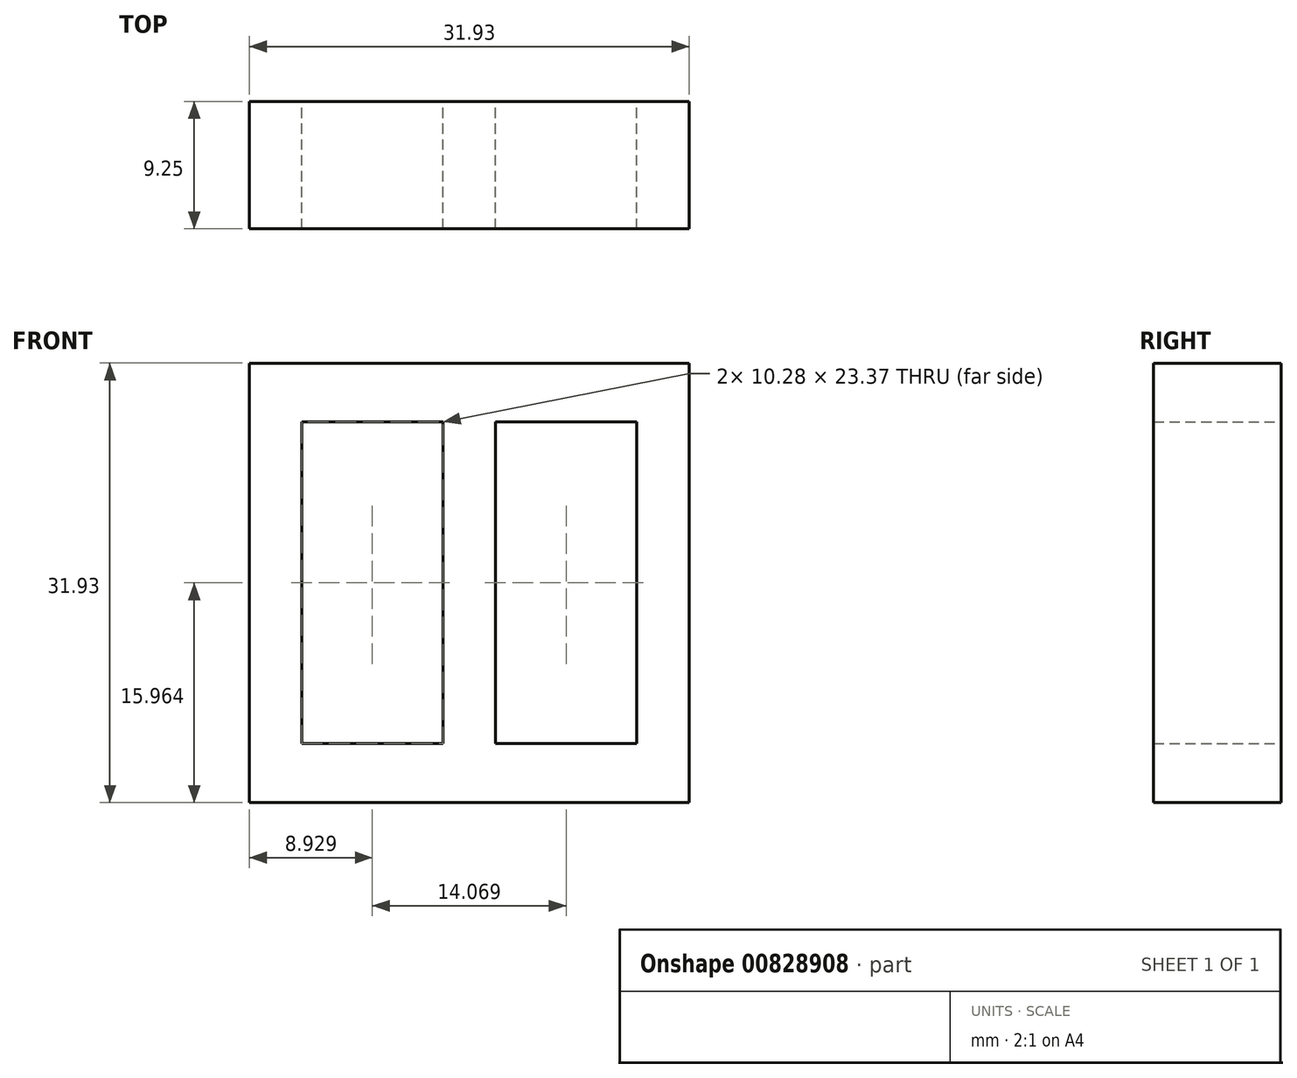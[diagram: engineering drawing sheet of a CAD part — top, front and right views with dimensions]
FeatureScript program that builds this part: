
annotation { "Feature Type Name" : "Feature", "Feature Type Description" : "" }
export const myFeature = defineFeature(function(context is Context, id is Id, definition is map)
    precondition{}
    {
        {
            var Q0;
            Q0=qCreatedBy(makeId("Front.planeOp"),FACE);
            var sketch = newSketch(context, id + "F0", { "sketchPlane" : qUnion([Q0])});
            skLineSegment(sketch, "E0.bottom", {"start": v(0, 0) * mm, "end": v(31.93, 0) * mm});
            skLineSegment(sketch, "E0.top", {"start": v(0, 31.93) * mm, "end": v(31.93, 31.93) * mm});
            skLineSegment(sketch, "E0.left", {"start": v(0, 0) * mm, "end": v(0, 31.93) * mm});
            skLineSegment(sketch, "E0.right", {"start": v(31.93, 0) * mm, "end": v(31.93, 31.93) * mm});
            skLineSegment(sketch, "E1.bottom", {"start": v(14.07, 4.28) * mm, "end": v(3.79, 4.28) * mm});
            skLineSegment(sketch, "E1.top", {"start": v(14.07, 27.65) * mm, "end": v(3.79, 27.65) * mm});
            skLineSegment(sketch, "E1.left", {"start": v(14.07, 4.28) * mm, "end": v(14.07, 27.65) * mm});
            skLineSegment(sketch, "E1.right", {"start": v(3.79, 4.28) * mm, "end": v(3.79, 27.65) * mm});
            skPoint(sketch, "E1.middle", {"position": v(8.93, 15.96) * mm});
            skPoint(sketch, "E1.middle.positionSnap0", {"position": v(31.93, 15.96) * mm});
            skPoint(sketch, "E1.centerSnap0", {"position": v(31.93, 15.96) * mm});
            skLineSegment(sketch, "E2.bottom", {"start": v(28.14, 4.28) * mm, "end": v(17.86, 4.28) * mm});
            skLineSegment(sketch, "E2.top", {"start": v(28.14, 27.65) * mm, "end": v(17.86, 27.65) * mm});
            skLineSegment(sketch, "E2.left", {"start": v(28.14, 4.28) * mm, "end": v(28.14, 27.65) * mm});
            skLineSegment(sketch, "E2.right", {"start": v(17.86, 4.28) * mm, "end": v(17.86, 27.65) * mm});
            skPoint(sketch, "E2.middle", {"position": v(23, 15.96) * mm});
            skLineSegment(sketch, "E3", {"start": v(14.07, 15.96) * mm, "end": v(17.86, 15.96) * mm, "construction": true});
            skLineSegment(sketch, "E4", {"start": v(3.79, 15.96) * mm, "end": v(0, 15.96) * mm, "construction": true});
            skLineSegment(sketch, "E5", {"start": v(28.14, 15.96) * mm, "end": v(31.93, 15.96) * mm, "construction": true});
            skSolve(sketch);
        }
        {
            var Q0;
            Q0=makeQuery(id+"F0.imprint","IMPRINT",FACE,{"disambiguationData":[TD([[makeQuery(id+"F0.imprint","IMPRINT",EDGE,{"derivedFrom":sQuery(id+"F0.wireOp",EDGE,"E0.bottom")}),1.0]])]});
            extrude(context, id + "F1", {"entities" : qUnion([Q0]), "depth" : 9.25 * mm, "offsetDistance" : 25.4 * mm});
        }
    });
